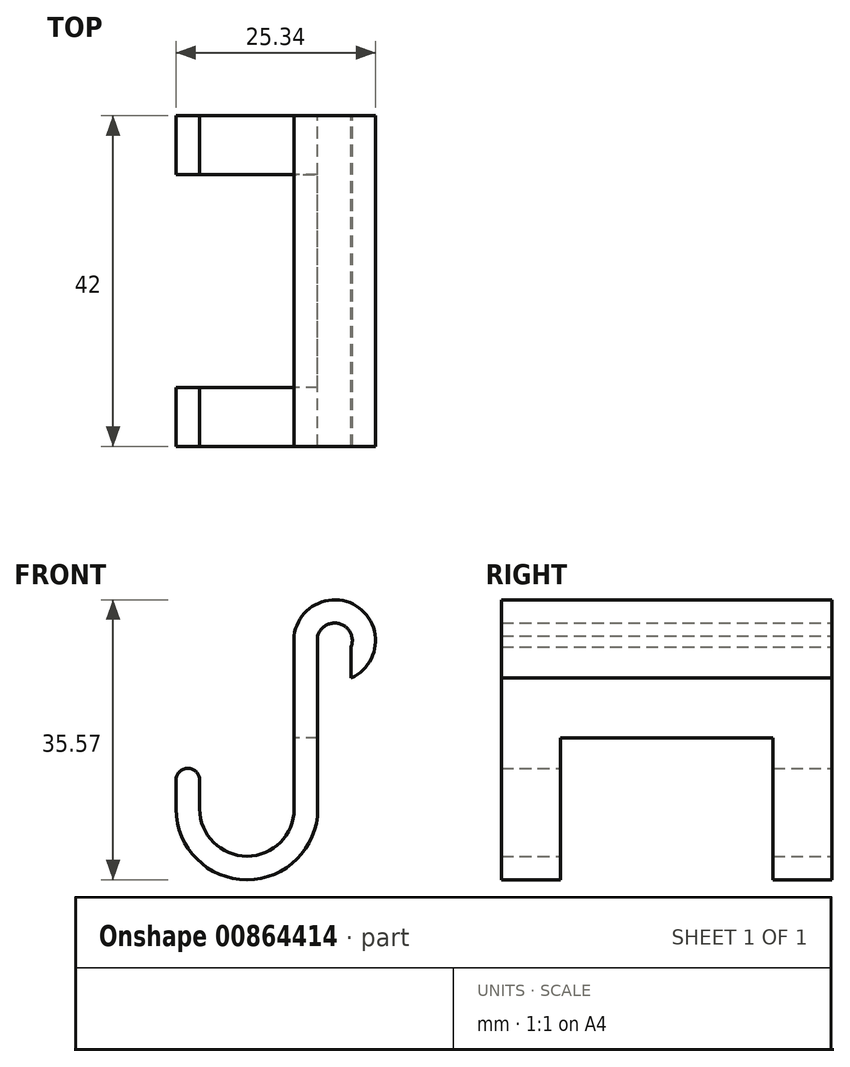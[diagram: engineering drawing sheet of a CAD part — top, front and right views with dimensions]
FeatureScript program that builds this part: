
annotation { "Feature Type Name" : "Feature", "Feature Type Description" : "" }
export const myFeature = defineFeature(function(context is Context, id is Id, definition is map)
    precondition{}
    {
        {
            var Q0;
            Q0=qCreatedBy(makeId("Front.planeOp"),FACE);
            var sketch = newSketch(context, id + "F0", { "sketchPlane" : qUnion([Q0])});
            skLineSegment(sketch, "E0", {"start": v(0, 13.54) * mm, "end": v(0, 0) * mm});
            skLineSegment(sketch, "E1", {"start": v(5.15, 27.3) * mm, "end": v(5.15, -24.51) * mm, "construction": true});
            skLineSegment(sketch, "E2", {"start": v(-12, 22.6) * mm, "end": v(-12, -20.7) * mm, "construction": true});
            skLineSegment(sketch, "E3", {"start": v(-15, 19.54) * mm, "end": v(-15, -24.51) * mm, "construction": true});
            skLineSegment(sketch, "E4", {"start": v(7.25, 36.22) * mm, "end": v(7.25, -59.06) * mm, "construction": true});
            skArc(sketch, "E5", {"start": v(3, 22) * mm, "mid": v(5.84, 23.5) * mm, "end": v(7.25, 20.61) * mm});
            skLineSegment(sketch, "E6", {"start": v(10.25, 56.97) * mm, "end": v(10.25, -48.9) * mm, "construction": true});
            skLineSegment(sketch, "E7", {"start": v(0, 13.54) * mm, "end": v(0, 32.24) * mm});
            skArc(sketch, "E8", {"start": v(0, 22) * mm, "mid": v(8.23, 25.55) * mm, "end": v(7.25, 16.64) * mm});
            skLineSegment(sketch, "E9", {"start": v(7.25, 16.64) * mm, "end": v(7.25, 20.61) * mm});
            skLineSegment(sketch, "E10", {"start": v(0, 13.54) * mm, "end": v(0, 22) * mm});
            skLineSegment(sketch, "E11", {"start": v(-6, 20.63) * mm, "end": v(-6, -40.15) * mm, "construction": true});
            skArc(sketch, "E12", {"start": v(0, 0) * mm, "mid": v(-6, -6) * mm, "end": v(-12, 0) * mm});
            skLineSegment(sketch, "E13", {"start": v(-12, 0) * mm, "end": v(-12, 3.66) * mm});
            skLineSegment(sketch, "E14", {"start": v(-12, 3.66) * mm, "end": v(-12, 0) * mm});
            skArc(sketch, "E15", {"start": v(-12, 3.66) * mm, "mid": v(-13.5, 5.16) * mm, "end": v(-15, 3.66) * mm});
            skArc(sketch, "E16", {"start": v(3, 0) * mm, "mid": v(-6, -9) * mm, "end": v(-15, 0) * mm, "construction": true});
            skLineSegment(sketch, "E17", {"start": v(-15, 0) * mm, "end": v(-15, 3.66) * mm});
            skLineSegment(sketch, "E18", {"start": v(3, 22) * mm, "end": v(3, 0) * mm});
            skLineSegment(sketch, "E19", {"start": v(-8.52, -8.64) * mm, "end": v(-10, -8.06) * mm});
            skArc(sketch, "E20", {"start": v(3, 0) * mm, "mid": v(-6, -9) * mm, "end": v(-15, 0) * mm});
            skSolve(sketch);
        }
        {
            var Q0;
            Q0 = qSketchRegion(id + "F0", true);
            extrude(context, id + "F1", {"entities" : qUnion([Q0]), "depth" : 42 * mm, "offsetDistance" : 25 * mm});
        }
        {
            var Q0;
            Q0=makeQuery(id+"F1.opExtrude","SWEPT_FACE",FACE,{"disambiguationData":[OSD([sQuery(id+"F0.wireOp",EDGE,"E0"),sQuery(id+"F0.wireOp",EDGE,"E10")])]});
            var sketch = newSketch(context, id + "F2", { "sketchPlane" : qUnion([Q0])});
            skLineSegment(sketch, "E21", {"start": v(68.71, 9) * mm, "end": v(-20.4, 9) * mm, "construction": true});
            skLineSegment(sketch, "E22", {"start": v(-20.4, 9) * mm, "end": v(-39.88, 16.9) * mm, "construction": true});
            skLineSegment(sketch, "E23", {"start": v(7.5, 45.22) * mm, "end": v(7.5, -26.34) * mm, "construction": true});
            skLineSegment(sketch, "E24", {"start": v(34.5, 47.15) * mm, "end": v(34.5, -26.34) * mm, "construction": true});
            skLineSegment(sketch, "E25", {"start": v(7.5, -16.11) * mm, "end": v(7.5, 9) * mm});
            skLineSegment(sketch, "E26", {"start": v(7.5, 9) * mm, "end": v(34.5, 9) * mm});
            skLineSegment(sketch, "E27", {"start": v(34.5, 9) * mm, "end": v(34.5, -18.63) * mm});
            skLineSegment(sketch, "E28", {"start": v(34.5, -18.63) * mm, "end": v(7.5, -16.11) * mm});
            skSolve(sketch);
        }
        {
            var Q0;
            Q0 = qSketchRegion(id + "F2", true);
            extrude(context, id + "F3", {"entities" : qUnion([Q0]), "operationType" : NewBodyOperationType.REMOVE, "endBound" : BoundingType.SYMMETRIC, "oppositeDirection" : true, "depth" : 33 * mm, "offsetDistance" : 25 * mm});
        }
    });
